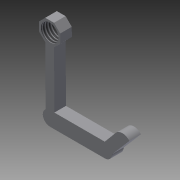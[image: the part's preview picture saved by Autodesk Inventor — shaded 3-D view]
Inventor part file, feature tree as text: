
AUTODESK INVENTOR PART (.ipt)
format: ipt  version: 2015 SP2 (Build 190223200, 223)  size: 124,928 bytes
history: native  units: mm
features: sketch x15, extrude x6, plane x5, hole x1, thread x1
ambient origin geometry x8: Origin, YZ Plane, XZ Plane, XY Plane, X Axis, Y Axis, Z Axis, Center Point
bodies: Solid1 (feature_tree)
feature tree (28):
  sketch  "Sketch1"  dims[d4=2.0mm d5=0.0mm d6=10.0mm d7=0.0mm]
  sketch  "Sketch2"  dims[d10=2.0mm d11=0.0mm d15=2.0mm d16=0.0mm]
  plane  "Work Plane1"
  extrude  "Extrusion2"  Depth=10.0mm TaperAngle=0.0deg
  plane  "Work Plane2"
  extrude  "Extrusion3"  Depth=2.0mm TaperAngle=0.0deg
  sketch  "Sketch5"  dims[d24=3.0mm d25=6.0mm d26=4.0mm d27=2.0mm d28=90.0deg d29=8.0mm d30=20.594885mm d31=10.0mm d32=0.0mm]
  sketch  "Sketch6"
  extrude  "Extrusion4"  Depth=2.0mm TaperAngle=0.0deg
  sketch  "Sketch8"
  sketch  "Sketch9"
  sketch  "Sketch11"
  sketch  "Sketch12"
  plane  "Work Plane3"
  extrude  "Extrusion6"  Depth=2.0mm TaperAngle=0.0deg
  plane  "Work Plane4"
  extrude  "Extrusion7"  Depth=10.0mm TaperAngle=0.0deg
  plane  "Work Plane5"
  extrude  "Extrusion8"  [1 undecoded]
  sketch  "Sketch16"
  hole  "Hole1"  [1 undecoded]
  thread  "Thread2"  [1 undecoded]
  sketch  "Sketch3"  dims[d17=2.483mm d18=2.0mm d19=0.0mm]
  sketch  "Sketch4"  dims[d20=8.726646mm d21=2.0mm d22=0.0mm]
  sketch  "Sketch7"
  sketch  "Sketch13"
  sketch  "Sketch14"
  sketch  "Sketch15"
note: 3 required parameter values undecoded (feature->parameter linkage not recoverable at this tier; creation-order binding heuristic only, values carry confidence <= 0.55)
